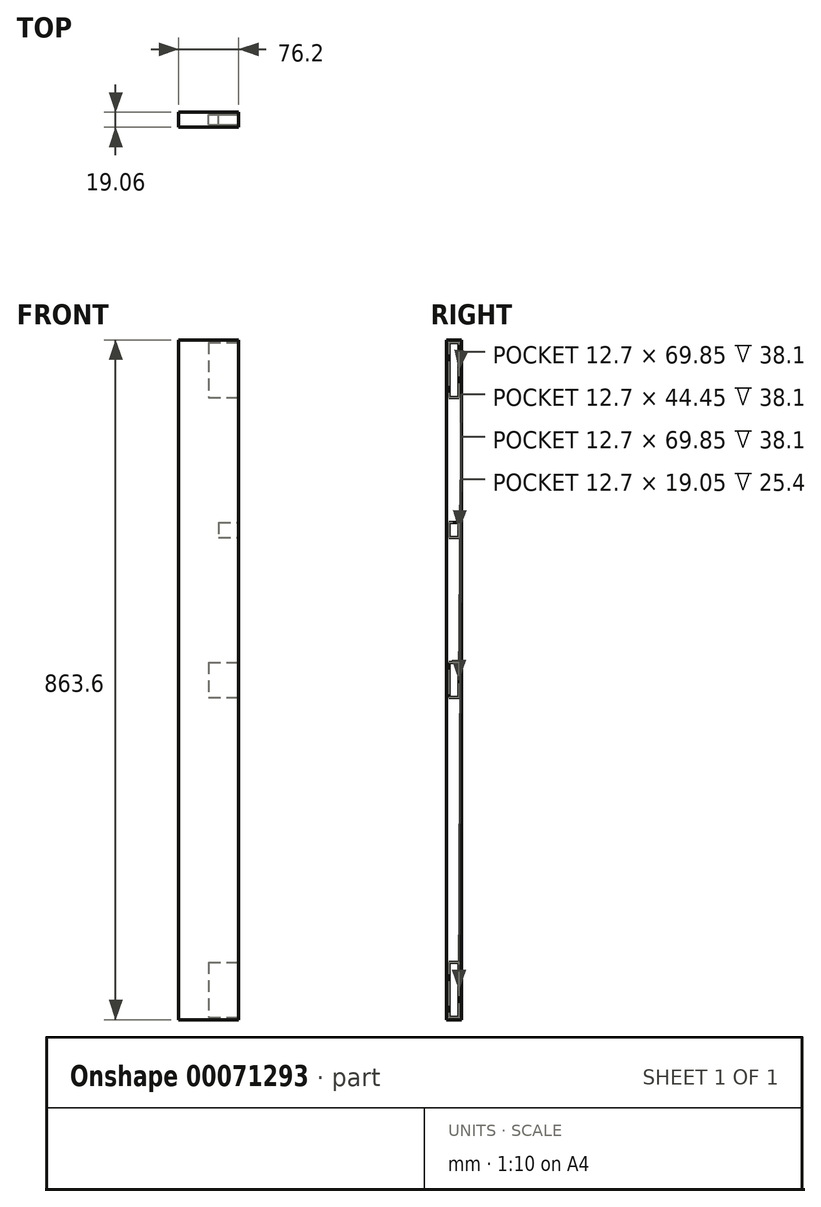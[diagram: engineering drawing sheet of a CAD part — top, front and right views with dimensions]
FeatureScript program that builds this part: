
annotation { "Feature Type Name" : "Feature", "Feature Type Description" : "" }
export const myFeature = defineFeature(function(context is Context, id is Id, definition is map)
    precondition{}
    {
        {
            var Q0;
            Q0=qCreatedBy(makeId("Front.planeOp"),FACE);
            var sketch = newSketch(context, id + "F0", { "sketchPlane" : qUnion([Q0])});
            skLineSegment(sketch, "E0.bottom", {"start": v(-38.1, 431.8) * mm, "end": v(38.1, 431.8) * mm});
            skLineSegment(sketch, "E0.top", {"start": v(-38.1, -431.8) * mm, "end": v(38.1, -431.8) * mm});
            skLineSegment(sketch, "E0.left", {"start": v(-38.1, 431.8) * mm, "end": v(-38.1, -431.8) * mm});
            skLineSegment(sketch, "E0.right", {"start": v(38.1, 431.8) * mm, "end": v(38.1, -431.8) * mm});
            skSolve(sketch);
        }
        {
            var Q0;
            Q0=makeQuery(id+"F0.imprint","IMPRINT",FACE,{"disambiguationData":[TD([[makeQuery(id+"F0.imprint","IMPRINT",EDGE,{"derivedFrom":sQuery(id+"F0.wireOp",EDGE,"E0.bottom")}),-1.0]])]});
            extrude(context, id + "F1", {"entities" : qUnion([Q0]), "endBound" : BoundingType.SYMMETRIC, "depth" : 19.05 * mm});
        }
        {
            var Q0;
            Q0=makeQuery(id+"F1.opExtrude","SWEPT_FACE",FACE,{"disambiguationData":[OSD([sQuery(id+"F0.wireOp",EDGE,"E0.right")])]});
            var sketch = newSketch(context, id + "F2", { "sketchPlane" : qUnion([Q0])});
            skLineSegment(sketch, "E1.bottom", {"start": v(-6.35, 428.63) * mm, "end": v(6.35, 428.63) * mm});
            skLineSegment(sketch, "E1.top", {"start": v(-6.35, 358.78) * mm, "end": v(6.35, 358.78) * mm});
            skLineSegment(sketch, "E1.left", {"start": v(-6.35, 428.63) * mm, "end": v(-6.35, 358.78) * mm});
            skLineSegment(sketch, "E1.right", {"start": v(6.35, 428.63) * mm, "end": v(6.35, 358.78) * mm});
            skLineSegment(sketch, "E2.bottom", {"start": v(-6.35, -358.78) * mm, "end": v(6.35, -358.78) * mm});
            skLineSegment(sketch, "E2.top", {"start": v(-6.35, -428.63) * mm, "end": v(6.35, -428.63) * mm});
            skLineSegment(sketch, "E2.left", {"start": v(-6.35, -358.78) * mm, "end": v(-6.35, -428.63) * mm});
            skLineSegment(sketch, "E2.right", {"start": v(6.35, -358.78) * mm, "end": v(6.35, -428.63) * mm});
            skLineSegment(sketch, "E3.bottom", {"start": v(-6.35, 22.22) * mm, "end": v(6.35, 22.22) * mm});
            skLineSegment(sketch, "E3.top", {"start": v(-6.35, -22.23) * mm, "end": v(6.35, -22.23) * mm});
            skLineSegment(sketch, "E3.left", {"start": v(-6.35, 22.22) * mm, "end": v(-6.35, -22.23) * mm});
            skLineSegment(sketch, "E3.right", {"start": v(6.35, 22.22) * mm, "end": v(6.35, -22.23) * mm});
            skSolve(sketch);
        }
        {
            var Q0;
            Q0=makeQuery(id+"F2.imprint","IMPRINT",FACE,{"disambiguationData":[TD([[makeQuery(id+"F2.imprint","IMPRINT",EDGE,{"derivedFrom":sQuery(id+"F2.wireOp",EDGE,"E1.bottom")}),-1.0]])]});
            extrude(context, id + "F3", {"entities" : qUnion([Q0]), "operationType" : NewBodyOperationType.REMOVE, "oppositeDirection" : true, "depth" : 38.1 * mm});
        }
        {
            var Q0;
            Q0=makeQuery(id+"F2.imprint","IMPRINT",FACE,{"disambiguationData":[TD([[makeQuery(id+"F2.imprint","IMPRINT",EDGE,{"derivedFrom":sQuery(id+"F2.wireOp",EDGE,"E3.bottom")}),-1.0]])]});
            extrude(context, id + "F4", {"entities" : qUnion([Q0]), "operationType" : NewBodyOperationType.REMOVE, "oppositeDirection" : true, "depth" : 38.1 * mm});
        }
        {
            var Q0;
            Q0=makeQuery(id+"F2.imprint","IMPRINT",FACE,{"disambiguationData":[TD([[makeQuery(id+"F2.imprint","IMPRINT",EDGE,{"derivedFrom":sQuery(id+"F2.wireOp",EDGE,"E2.bottom")}),-1.0]])]});
            extrude(context, id + "F5", {"entities" : qUnion([Q0]), "operationType" : NewBodyOperationType.REMOVE, "oppositeDirection" : true, "depth" : 38.1 * mm});
        }
        {
            var Q0;
            Q0=makeQuery(id+"F2.imprint","IMPRINT",FACE,{"disambiguationData":[TD([[makeQuery(id+"F2.imprint","IMPRINT",EDGE,{"derivedFrom":sQuery(id+"F2.wireOp",EDGE,"E1.bottom")}),1.0]])]});
            var sketch = newSketch(context, id + "F6", { "sketchPlane" : qUnion([Q0])});
            skLineSegment(sketch, "E4.bottom", {"start": v(-6.35, 200.02) * mm, "end": v(6.35, 200.02) * mm});
            skLineSegment(sketch, "E4.top", {"start": v(-6.35, 180.97) * mm, "end": v(6.35, 180.97) * mm});
            skLineSegment(sketch, "E4.left", {"start": v(-6.35, 200.02) * mm, "end": v(-6.35, 180.97) * mm});
            skLineSegment(sketch, "E4.right", {"start": v(6.35, 200.02) * mm, "end": v(6.35, 180.97) * mm});
            skSolve(sketch);
        }
        {
            var Q0;
            Q0 = qSketchRegion(id + "F6", true);
            extrude(context, id + "F7", {"entities" : qUnion([Q0]), "operationType" : NewBodyOperationType.REMOVE, "oppositeDirection" : true, "depth" : 25.4 * mm});
        }
    });
